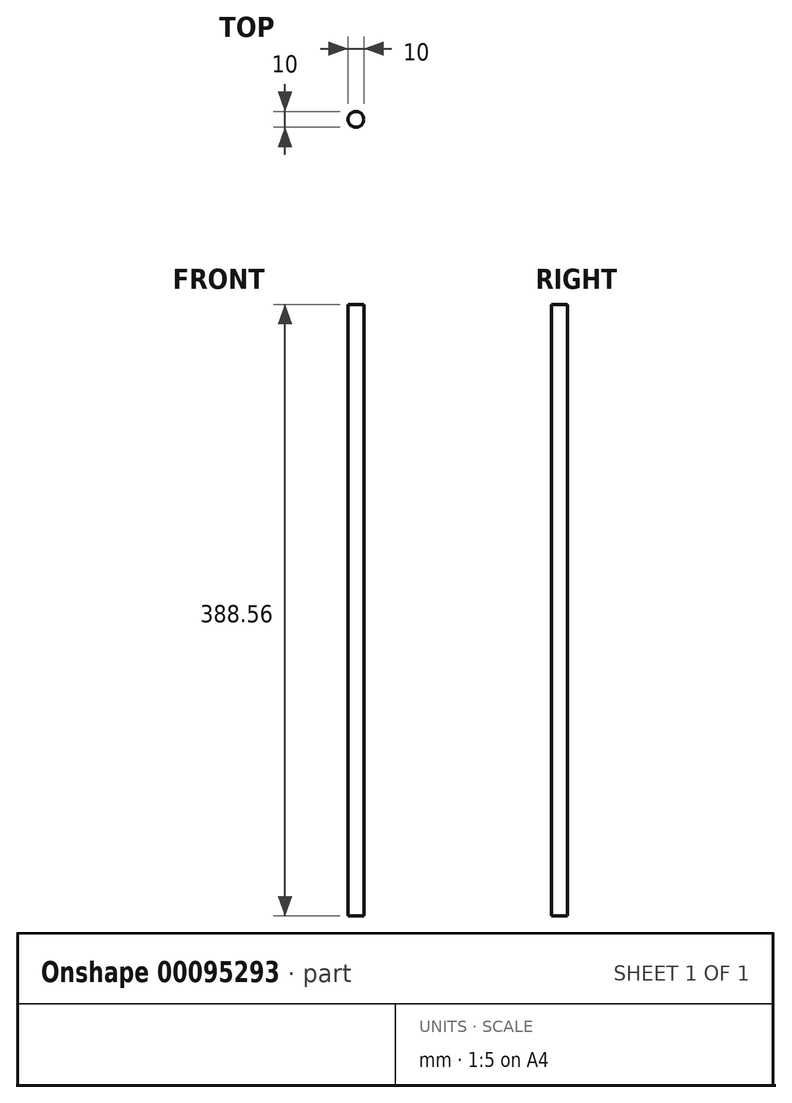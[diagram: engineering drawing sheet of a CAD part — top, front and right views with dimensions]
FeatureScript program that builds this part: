
annotation { "Feature Type Name" : "Feature", "Feature Type Description" : "" }
export const myFeature = defineFeature(function(context is Context, id is Id, definition is map)
    precondition{}
    {
        {
            var Q0;
            Q0=qCreatedBy(makeId("Top.planeOp"),FACE);
            var sketch = newSketch(context, id + "F0", { "sketchPlane" : qUnion([Q0])});
            skCircle(sketch, "E0", {"center": v(0, 0) * mm, "radius": 5 * mm});
            skSolve(sketch);
        }
        {
            var Q0;
            Q0=qSketchRegion(id+"F0",true);
            extrude(context, id + "F1", {"entities" : qUnion([Q0]), "depth" : 388.56 * mm});
        }
    });
